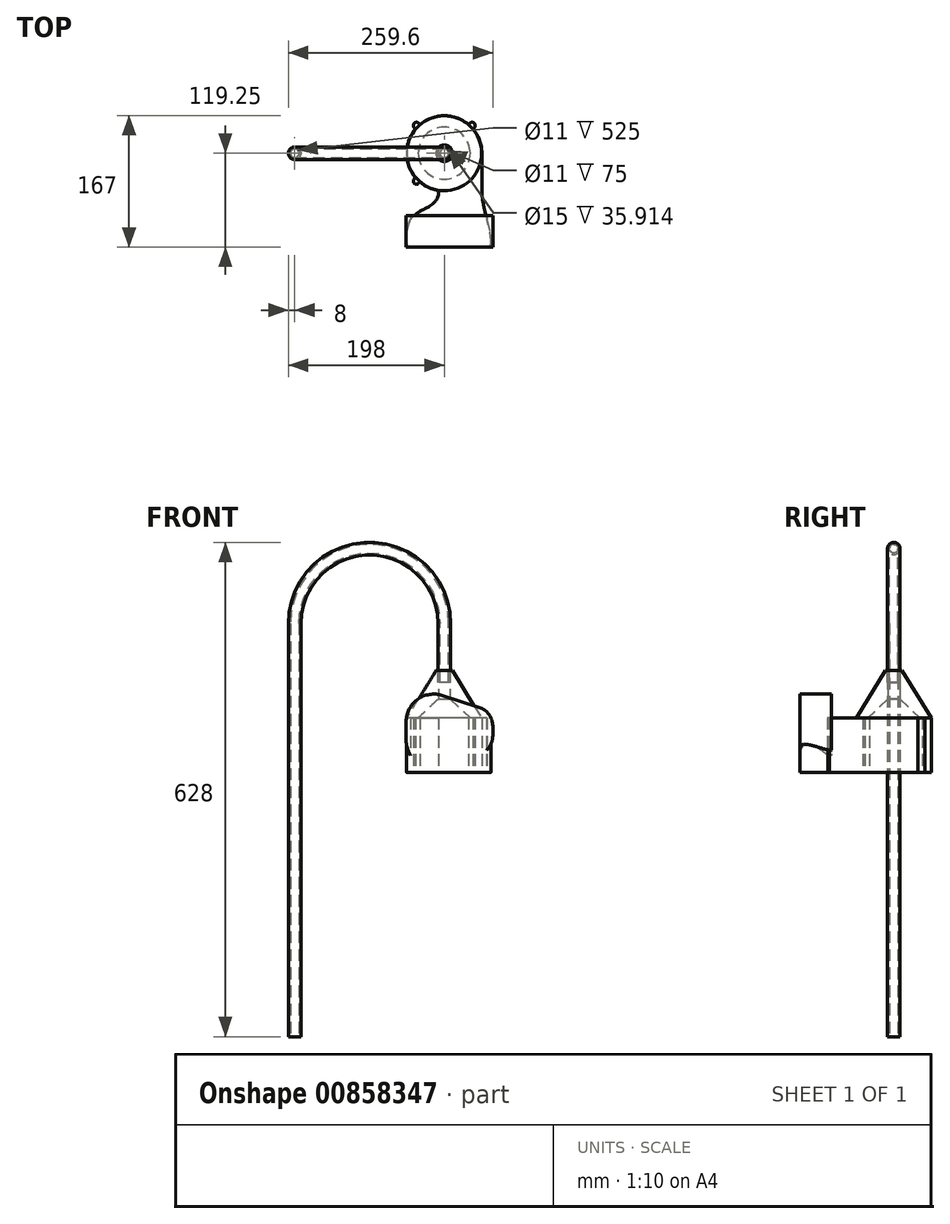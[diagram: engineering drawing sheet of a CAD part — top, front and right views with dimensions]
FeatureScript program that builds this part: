
annotation { "Feature Type Name" : "Feature", "Feature Type Description" : "" }
export const myFeature = defineFeature(function(context is Context, id is Id, definition is map)
    precondition{}
    {
        {
            var Q0;
            Q0=qCreatedBy(makeId("Top.planeOp"),FACE);
            var sketch = newSketch(context, id + "F0", { "sketchPlane" : qUnion([Q0])});
            skArc(sketch, "E0", {"start": v(-9.64, -46.77) * mm, "mid": v(-30.16, 37.02) * mm, "end": v(47.75, 0) * mm});
            skLineSegment(sketch, "E1", {"start": v(47.75, 0) * mm, "end": v(47.75, -49.79) * mm});
            skArc(sketch, "E2", {"start": v(-9.64, -46.77) * mm, "mid": v(-7.9, -47.84) * mm, "end": v(-7.25, -49.79) * mm});
            skLineSegment(sketch, "E3", {"start": v(54.25, -119.25) * mm, "end": v(-42.76, -119.25) * mm});
            skArc(sketch, "E4", {"start": v(-42.76, -119.25) * mm, "mid": v(-46.2, -117.88) * mm, "end": v(-47.75, -114.52) * mm});
            skFitSpline(sketch, "E5", {"points": [v(-47.75, -114.52) * mm, v(-42.8, -84.25) * mm, v(-21.9, -69.06) * mm, v(-10.12, -59.38) * mm, v(-7.25, -49.79) * mm], "startDerivative": vector(-3.9, 71.7) * mm, "endDerivative": vector(2.07, 72.19) * mm});
            skLineSegment(sketch, "E6", {"start": v(-47.75, 0) * mm, "end": v(-47.75, -114.52) * mm, "construction": true});
            skArc(sketch, "E7", {"start": v(54.25, -119.25) * mm, "mid": v(57.79, -117.79) * mm, "end": v(59.25, -114.25) * mm});
            skFitSpline(sketch, "E8", {"points": [v(59.25, -114.25) * mm, v(54.11, -83.4) * mm, v(47.75, -49.79) * mm], "startDerivative": vector(0, 59.89) * mm, "endDerivative": vector(0, 48.46) * mm});
            skFitSpline(sketch, "E9", {"points": [v(54.11, -83.4) * mm, v(53.47, -80.79) * mm], "startDerivative": vector(-1.52, 7.42) * mm, "endDerivative": vector(-1.52, 7.42) * mm});
            skLineSegment(sketch, "E10", {"start": v(-35.36, -35.36) * mm, "end": v(35.36, 35.36) * mm, "construction": true});
            skArc(sketch, "E11", {"start": v(32.53, 38.18) * mm, "mid": v(38.18, 38.18) * mm, "end": v(38.18, 32.53) * mm});
            skArc(sketch, "E12", {"start": v(-38.18, -32.53) * mm, "mid": v(-38.18, -38.18) * mm, "end": v(-32.53, -38.18) * mm});
            skLineSegment(sketch, "E13", {"start": v(0, 0) * mm, "end": v(-35.36, 35.36) * mm, "construction": true});
            skArc(sketch, "E14", {"start": v(-38.18, 32.53) * mm, "mid": v(-38.18, 38.18) * mm, "end": v(-32.53, 38.18) * mm});
            skLineSegment(sketch, "E15", {"start": v(38.18, 32.53) * mm, "end": v(36.47, 30.82) * mm});
            skLineSegment(sketch, "E16", {"start": v(32.53, 38.18) * mm, "end": v(30.82, 36.47) * mm});
            skLineSegment(sketch, "E17", {"start": v(-32.53, 38.18) * mm, "end": v(-30.82, 36.47) * mm});
            skLineSegment(sketch, "E18", {"start": v(-38.18, 32.53) * mm, "end": v(-36.47, 30.82) * mm});
            skLineSegment(sketch, "E19", {"start": v(-38.18, -32.53) * mm, "end": v(-36.47, -30.82) * mm});
            skLineSegment(sketch, "E20", {"start": v(-32.53, -38.18) * mm, "end": v(-30.82, -36.47) * mm});
            skSolve(sketch);
        }
        {
            var Q0;
            Q0 = qSketchRegion(id + "F0", true);
            extrude(context, id + "F1", {"entities" : qUnion([Q0]), "depth" : 69.5 * mm, "offsetDistance" : 25 * mm});
        }
        {
            var Q0;
            Q0=makeQuery(id+"F1.opExtrude","SWEPT_FACE",FACE,{"disambiguationData":[OSD([sQuery(id+"F0.wireOp",EDGE,"E3")])]});
            var sketch = newSketch(context, id + "F2", { "sketchPlane" : qUnion([Q0])});
            skLineSegment(sketch, "E21", {"start": v(-48.4, 64.7) * mm, "end": v(-48.4, 41) * mm});
            skLineSegment(sketch, "E22", {"start": v(-2.64, 7.7) * mm, "end": v(44.28, 22.85) * mm});
            skLineSegment(sketch, "E23", {"start": v(61.6, 46.64) * mm, "end": v(61.6, 59.06) * mm});
            skLineSegment(sketch, "E24", {"start": v(44.28, 82.85) * mm, "end": v(-2.64, 98) * mm});
            skLineSegment(sketch, "E25", {"start": v(-48.4, 52.85) * mm, "end": v(61.6, 52.85) * mm, "construction": true});
            skPoint(sketch, "E26.visualSharp", {"position": v(-48.4, 112.77) * mm});
            skArc(sketch, "E26.filletArc", {"start": v(-2.64, 98) * mm, "mid": v(-34, 93) * mm, "end": v(-48.4, 64.7) * mm});
            skPoint(sketch, "E27.visualSharp", {"position": v(-48.4, -7.08) * mm});
            skArc(sketch, "E27.filletArc", {"start": v(-48.4, 41) * mm, "mid": v(-34, 12.7) * mm, "end": v(-2.64, 7.7) * mm});
            skPoint(sketch, "E28.visualSharp", {"position": v(61.6, 77.25) * mm});
            skArc(sketch, "E28.filletArc", {"start": v(61.6, 59.06) * mm, "mid": v(56.81, 73.77) * mm, "end": v(44.28, 82.85) * mm});
            skPoint(sketch, "E29.visualSharp", {"position": v(61.6, 28.44) * mm});
            skArc(sketch, "E29.filletArc", {"start": v(44.28, 22.85) * mm, "mid": v(56.81, 31.92) * mm, "end": v(61.6, 46.64) * mm});
            skSolve(sketch);
        }
        {
            var Q0;
            {var subQ9=sQuery(id+"F2.wireOp",EDGE,"E21");Q0=makeQuery(id+"F2.imprint","IMPRINT",FACE,{"disambiguationData":[TD([[makeQuery(id+"F2.imprint","IMPRINT",EDGE,{"derivedFrom":subQ9}),1.0]])]});}
            extrude(context, id + "F3", {"entities" : qUnion([Q0]), "operationType" : NewBodyOperationType.ADD, "oppositeDirection" : true, "depth" : 40 * mm, "offsetDistance" : 25 * mm});
        }
        {
            var Q0;
            Q0=qCreatedBy(makeId("Front.planeOp"),FACE);
            var sketch = newSketch(context, id + "F4", { "sketchPlane" : qUnion([Q0])});
            skLineSegment(sketch, "E30", {"start": v(0, 69.5) * mm, "end": v(0, 129.5) * mm, "construction": true});
            skLineSegment(sketch, "E31", {"start": v(7.5, 129.5) * mm, "end": v(7.5, 93.59) * mm});
            skLineSegment(sketch, "E32", {"start": v(7.5, 93.59) * mm, "end": v(33.05, 69.5) * mm});
            skLineSegment(sketch, "E33", {"start": v(33.05, 69.5) * mm, "end": v(47.5, 69.5) * mm});
            skLineSegment(sketch, "E34", {"start": v(47.5, 69.5) * mm, "end": v(10.5, 129.5) * mm});
            skLineSegment(sketch, "E35", {"start": v(10.5, 129.5) * mm, "end": v(7.5, 129.5) * mm});
            skSolve(sketch);
        }
        {
            var Q0;
            Q0 = qSketchRegion(id + "F4", true);
            var Q1;
            Q1=sQuery(id+"F4.wireOp",EDGE,"E30");
            revolve(context, id + "F5", {"operationType" : NewBodyOperationType.ADD, "surfaceOperationType" : NewSurfaceOperationType.NEW, "entities" : qUnion([Q0]), "axis" : qUnion([Q1]), "revolveType" : RevolveType.FULL});
        }
        {
            var Q0;
            Q0=qCreatedBy(makeId("Front.planeOp"),FACE);
            var sketch = newSketch(context, id + "F6", { "sketchPlane" : qUnion([Q0])});
            skLineSegment(sketch, "E36", {"start": v(0, 114.5) * mm, "end": v(0, 189.5) * mm});
            skArc(sketch, "E37", {"start": v(0, 189.5) * mm, "mid": v(-95, 284.5) * mm, "end": v(-190, 189.5) * mm});
            skLineSegment(sketch, "E38", {"start": v(-190, 189.5) * mm, "end": v(-190, -335.5) * mm});
            skSolve(sketch);
        }
        {
            var Q0;
            Q0=qCreatedBy(makeId("Top.planeOp"),FACE);
            var Q1;
            Q1=sQuery(id+"F6.wireOp",VERTEX,"E36.start");
            cPlane(context, id + "F7", {"entities" : qUnion([Q0, Q1]), "cplaneType" : CPlaneType.PLANE_POINT, "offset" : 25 * mm, "width" : 150 * mm, "height" : 150 * mm});
        }
        {
            var Q0;
            Q0=qCreatedBy(id+"F7.planeOp",FACE);
            var sketch = newSketch(context, id + "F8", { "sketchPlane" : qUnion([Q0])});
            skCircle(sketch, "E39", {"center": v(0, 0) * mm, "radius": 5.5 * mm});
            skCircle(sketch, "E40", {"center": v(0, 0) * mm, "radius": 8 * mm});
            skSolve(sketch);
        }
        {
            var Q0;
            Q0 = qSketchRegion(id + "F8", true);
            var Q1;
            Q1 = qConstructionFilter(qBodyType(qCreatedBy(id + "F6" ,EDGE), BodyType.WIRE), ConstructionObject.NO);
            sweep(context, id + "F9", {"profiles" : qUnion([Q0]), "path" : qUnion([Q1])});
        }
    });
